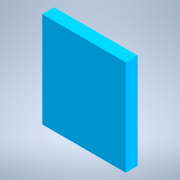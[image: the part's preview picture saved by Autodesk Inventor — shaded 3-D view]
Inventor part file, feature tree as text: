
AUTODESK INVENTOR PART (.ipt)
format: ipt  version: 2022.3 (Build 263350000, 350)  size: 99,840 bytes
history: native  units: in
note: dims shown in document units (in); Inventor stores cm internally (conversion verified against a paired STEP export)
features: extrude x1, sketch x1
ambient origin geometry x8: Origin, YZ Plane, XZ Plane, XY Plane, X Axis, Y Axis, Z Axis, Center Point
bodies: Solid1 (feature_tree)
feature tree (2):
  extrude  "Extrusion1"  Depth=0.8in
  sketch  "Sketch1"  dims[d0=0.7in d1=0.8in d2=0.1in d3=0.0in]
